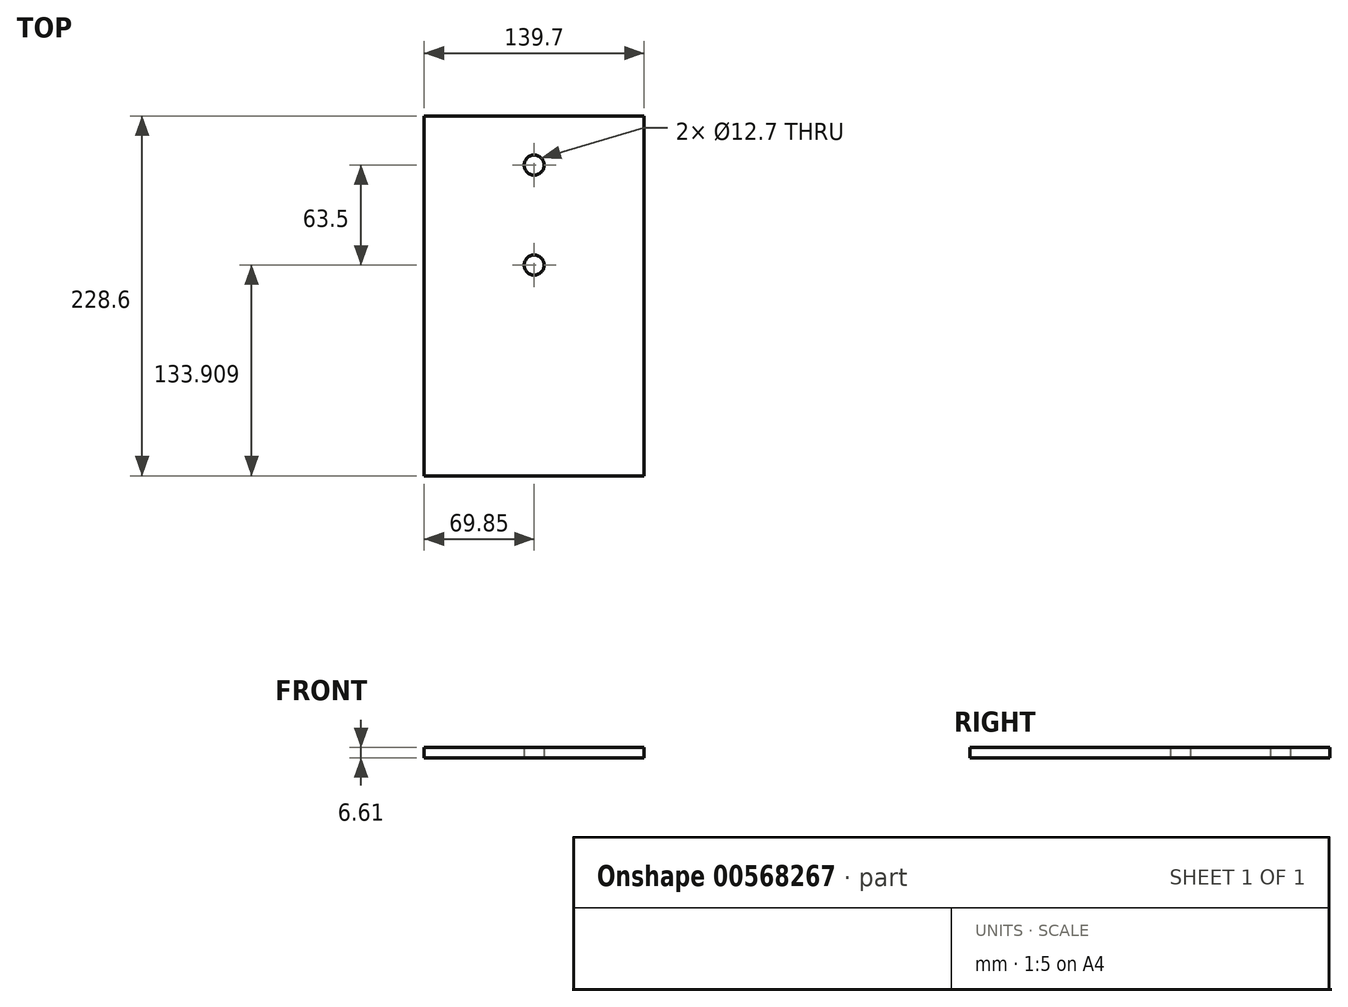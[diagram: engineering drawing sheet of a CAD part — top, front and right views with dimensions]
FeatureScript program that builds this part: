
annotation { "Feature Type Name" : "Feature", "Feature Type Description" : "" }
export const myFeature = defineFeature(function(context is Context, id is Id, definition is map)
    precondition{}
    {
        {
            var Q0;
            Q0=qCreatedBy(makeId("Top.planeOp"),FACE);
            var sketch = newSketch(context, id + "F0", { "sketchPlane" : qUnion([Q0])});
            skLineSegment(sketch, "E0.bottom", {"start": v(69.85, -114.3) * mm, "end": v(-69.85, -114.3) * mm});
            skLineSegment(sketch, "E0.top", {"start": v(69.85, 114.3) * mm, "end": v(-69.85, 114.3) * mm});
            skLineSegment(sketch, "E0.left", {"start": v(69.85, -114.3) * mm, "end": v(69.85, 114.3) * mm});
            skLineSegment(sketch, "E0.right", {"start": v(-69.85, -114.3) * mm, "end": v(-69.85, 114.3) * mm});
            skPoint(sketch, "E0.middle", {"position": v(0, 0) * mm});
            skCircle(sketch, "E1", {"center": v(0, 83.1) * mm, "radius": 6.35 * mm});
            skPoint(sketch, "E2.start.orphan", {"position": v(0, 114.3) * mm});
            skCircle(sketch, "E3", {"center": v(0, 19.6) * mm, "radius": 6.35 * mm});
            skSolve(sketch);
        }
        {
            var Q0;
            Q0 = qSketchRegion(id + "F0", true);
            extrude(context, id + "F1", {"entities" : qUnion([Q0]), "depth" : 6.61 * mm, "offsetDistance" : 25 * mm});
        }
    });
